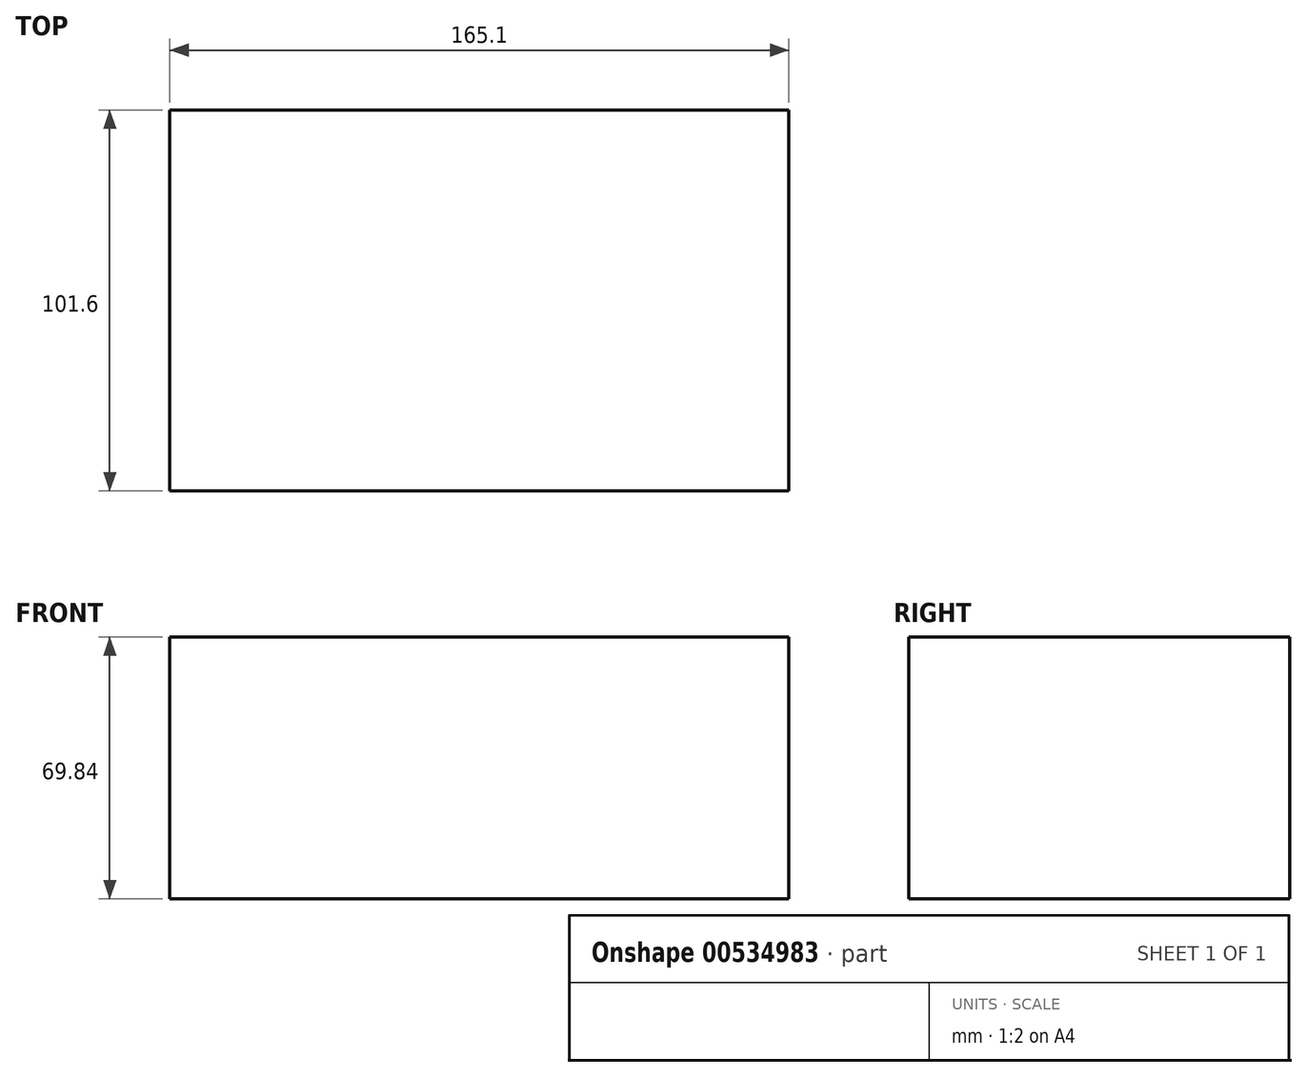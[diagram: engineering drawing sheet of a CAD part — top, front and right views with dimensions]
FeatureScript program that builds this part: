
annotation { "Feature Type Name" : "Feature", "Feature Type Description" : "" }
export const myFeature = defineFeature(function(context is Context, id is Id, definition is map)
    precondition{}
    {
        {
            var Q0;
            Q0=qCreatedBy(makeId("Front.planeOp"),FACE);
            var sketch = newSketch(context, id + "F0", { "sketchPlane" : qUnion([Q0])});
            skLineSegment(sketch, "E0.bottom", {"start": v(82.55, -34.92) * mm, "end": v(-82.55, -34.93) * mm});
            skLineSegment(sketch, "E0.top", {"start": v(82.55, 34.93) * mm, "end": v(-82.55, 34.92) * mm});
            skLineSegment(sketch, "E0.left", {"start": v(82.55, -34.92) * mm, "end": v(82.55, 34.93) * mm});
            skLineSegment(sketch, "E0.right", {"start": v(-82.55, -34.93) * mm, "end": v(-82.55, 34.92) * mm});
            skPoint(sketch, "E0.middle", {"position": v(0, 0) * mm});
            skSolve(sketch);
        }
        {
            var Q0;
            Q0 = qSketchRegion(id + "F0", true);
            extrude(context, id + "F1", {"entities" : qUnion([Q0]), "depth" : 101.6 * mm, "offsetDistance" : 25.4 * mm});
        }
    });
